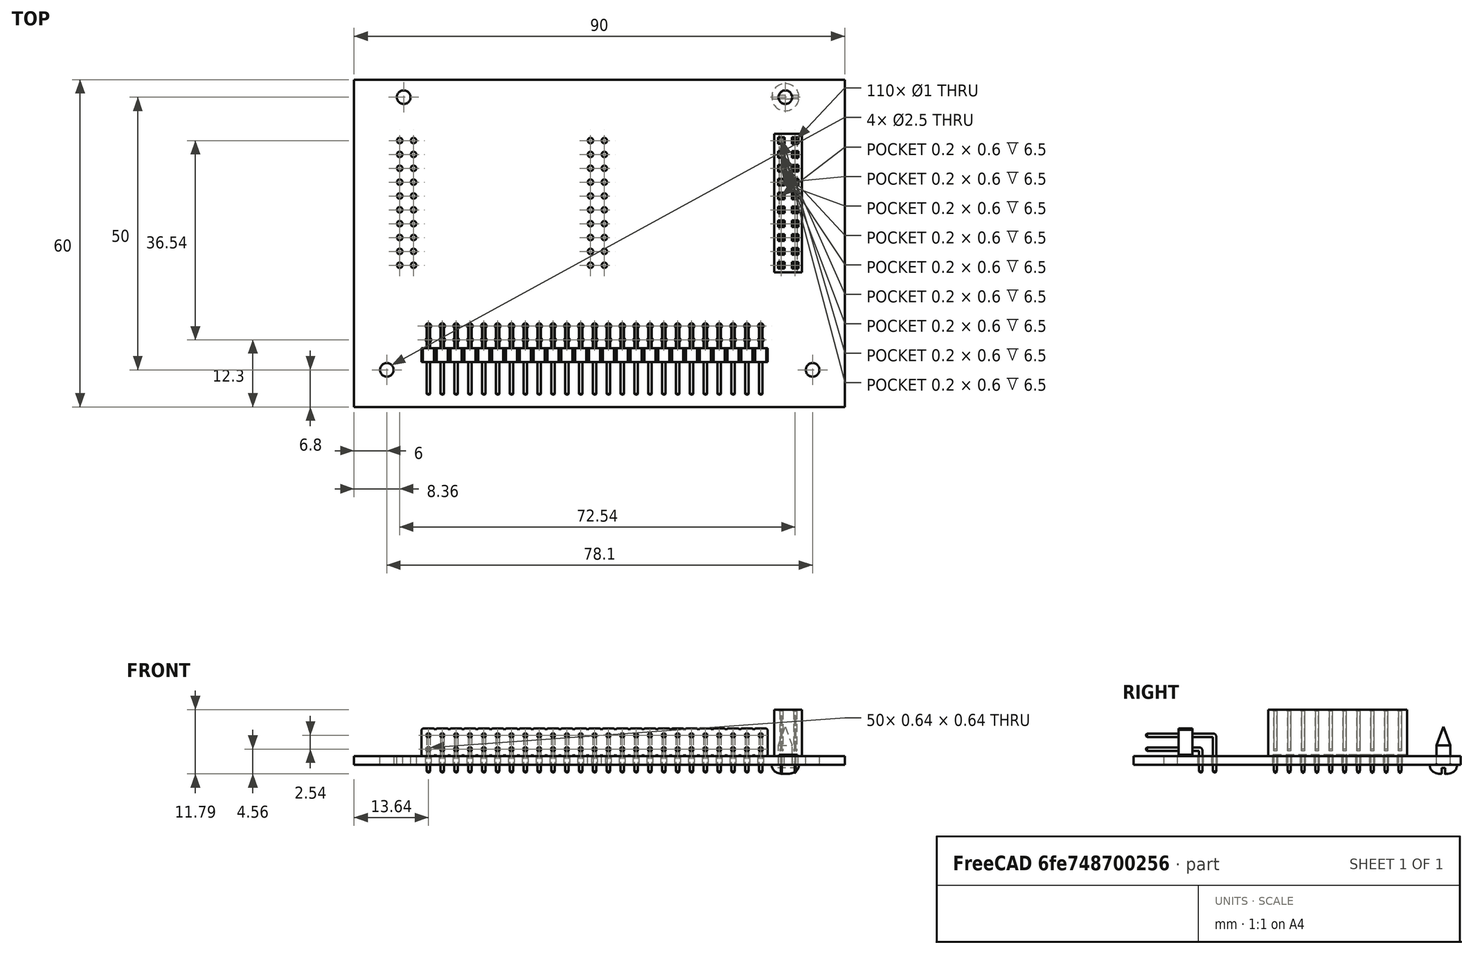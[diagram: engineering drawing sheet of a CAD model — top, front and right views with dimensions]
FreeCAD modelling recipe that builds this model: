
FCSTD DOCUMENT  (FreeCAD 1.0R39109 (Git))
Label: acd_dac_board
License: All rights reserved
LicenseURL: https://en.wikipedia.org/wiki/All_rights_reserved
objects: App::Part×6, App::Link×5, Part::Feature×4, PartDesign::CoordinateSystem×1, Sketcher::SketchObject×1
note: 7 computed .brp shape members not serialized (recipe doc carries the construction recipe); baked Part::Feature solids carry a one-line shape summary decoded from their .brp

FEATURE [PartDesign::CoordinateSystem] Local_CS_c5fe
  AttacherType = Attacher::AttachEngine3D
  MapMode = 2
FEATURE [Part::Feature] Pcb_c5fe
  shape: bbox 90 x 60 x 1.6 mm, 120 faces (baked)
FEATURE [Sketcher::SketchObject] PCB_Sketch_c5fe
  ArcFitTolerance = 1e-06
  FullyConstrained = false
  MakeInternals = false
  sketch-geometry (4):
    g0: LineSegment StartX=93.9 StartY=-71.9 StartZ=0 EndX=183.9 EndY=-71.9 EndZ=0
    g1: LineSegment StartX=183.9 StartY=-71.9 StartZ=0 EndX=183.9 EndY=-131.9 EndZ=0
    g2: LineSegment StartX=183.9 StartY=-131.9 StartZ=0 EndX=93.9 EndY=-131.9 EndZ=0
    g3: LineSegment StartX=93.9 StartY=-131.9 StartZ=0 EndX=93.9 EndY=-71.9 EndZ=0
  constraints (4):
    c: Coincident(g2,g3)
    c: Coincident(g0,g3)
    c: Coincident(g1,g2)
    c: Coincident(g0,g1)
FEATURE [App::Part] Board_Geoms_c5fe
  Group = -> [Pcb_c5fe,PCB_Sketch_c5fe]
  Origin = -> Origin
FEATURE [Part::Feature] Shape  label="J4_PinHeader_2x25_P254mm_Horizontal_27a54bd5aef3"
  Placement = pos=(168.5,-117.06,0) rot=(0,0,-1;1.5708rad)
  shape: bbox 63.5 x 12.9 x 8.08 mm, 1204 faces (baked)
FEATURE [Part::Feature] Shape001  label="J3_PinSocket_2x10_P2.54mm_Vertical_5a6bbbb15814"
  Placement = pos=(174.8,-83.06,0) rot=(0,0,1;0rad)
  shape: bbox 5.08 x 25.4 x 11.6 mm, 530 faces (baked)
FEATURE [App::Link] J3_PinSocket_2x10_P2_54mm_Vertical_5a6bbbb15814_ln_  label="J1_PinSocket_2x10_P2.54mm_Vertical_580dcfef748e"
  LinkPlacement = pos=(104.8,-83.06,0) rot=(0,0,1;0rad)
  LinkedObject = -> Shape001
  Placement = pos=(104.8,-83.06,0) rot=(0,0,1;0rad)
FEATURE [App::Link] J3_PinSocket_2x10_P2_54mm_Vertical_5a6bbbb15814_ln_001  label="J2_PinSocket_2x10_P2.54mm_Vertical_61ef51b03cdf"
  LinkPlacement = pos=(139.8,-83.06,0) rot=(0,0,1;0rad)
  LinkedObject = -> Shape001
  Placement = pos=(139.8,-83.06,0) rot=(0,0,1;0rad)
FEATURE [App::Part] Top_c5fe
  Group = -> [Shape,Shape001,J3_PinSocket_2x10_P2_54mm_Vertical_5a6bbbb15814_ln_,J3_PinSocket_2x10_P2_54mm_Vertical_5a6bbbb15814_ln_001]
  Origin = -> Origin003
FEATURE [App::Part] Step_Models_c5fe
  Group = -> [Top_c5fe]
  Origin = -> Origin002
FEATURE [Part::Feature] Shape002  label="REF_2.5 mmx7-Screw_fc498af58895"
  Placement = pos=(173,-75.1,-1.6) rot=(0,1,0;3.14159rad)
  shape: bbox 5 x 5 x 8.693 mm, 8 faces (baked)
FEATURE [App::Link] REF_2_5_mmx7_Screw_fc498af58895_ln_  label="REF_REF_2.5 mmx7-Screw_7bb2b2d65ce1"
  LinkPlacement = pos=(178,-125.1,-1.6) rot=(0,1,0;3.14159rad)
  LinkedObject = -> Shape002
  Placement = pos=(178,-125.1,-1.6) rot=(0,1,0;3.14159rad)
FEATURE [App::Link] REF_2_5_mmx7_Screw_fc498af58895_ln_001  label="REF_REF_2.5 mmx7-Screw_5b3bb718906a"
  LinkPlacement = pos=(99.9,-125.1,-1.6) rot=(0,1,0;3.14159rad)
  LinkedObject = -> Shape002
  Placement = pos=(99.9,-125.1,-1.6) rot=(0,1,0;3.14159rad)
FEATURE [App::Link] REF_2_5_mmx7_Screw_fc498af58895_ln_002  label="REF_REF_2.5 mmx7-Screw_1ec84486e3c5"
  LinkPlacement = pos=(103,-75.1,-1.6) rot=(0,1,0;3.14159rad)
  LinkedObject = -> Shape002
  Placement = pos=(103,-75.1,-1.6) rot=(0,1,0;3.14159rad)
FEATURE [App::Part] BotV_c5fe
  Group = -> [Shape002,REF_2_5_mmx7_Screw_fc498af58895_ln_,REF_2_5_mmx7_Screw_fc498af58895_ln_001,REF_2_5_mmx7_Screw_fc498af58895_ln_002]
  Origin = -> Origin007
FEATURE [App::Part] Step_Virtual_Models_c5fe
  Group = -> [BotV_c5fe]
  Origin = -> Origin005
FEATURE [App::Part] Board_c5fe  label="acd_dac_board"
  Group = -> [Local_CS_c5fe,Board_Geoms_c5fe,Step_Models_c5fe,Step_Virtual_Models_c5fe]
  Origin = -> Origin001
